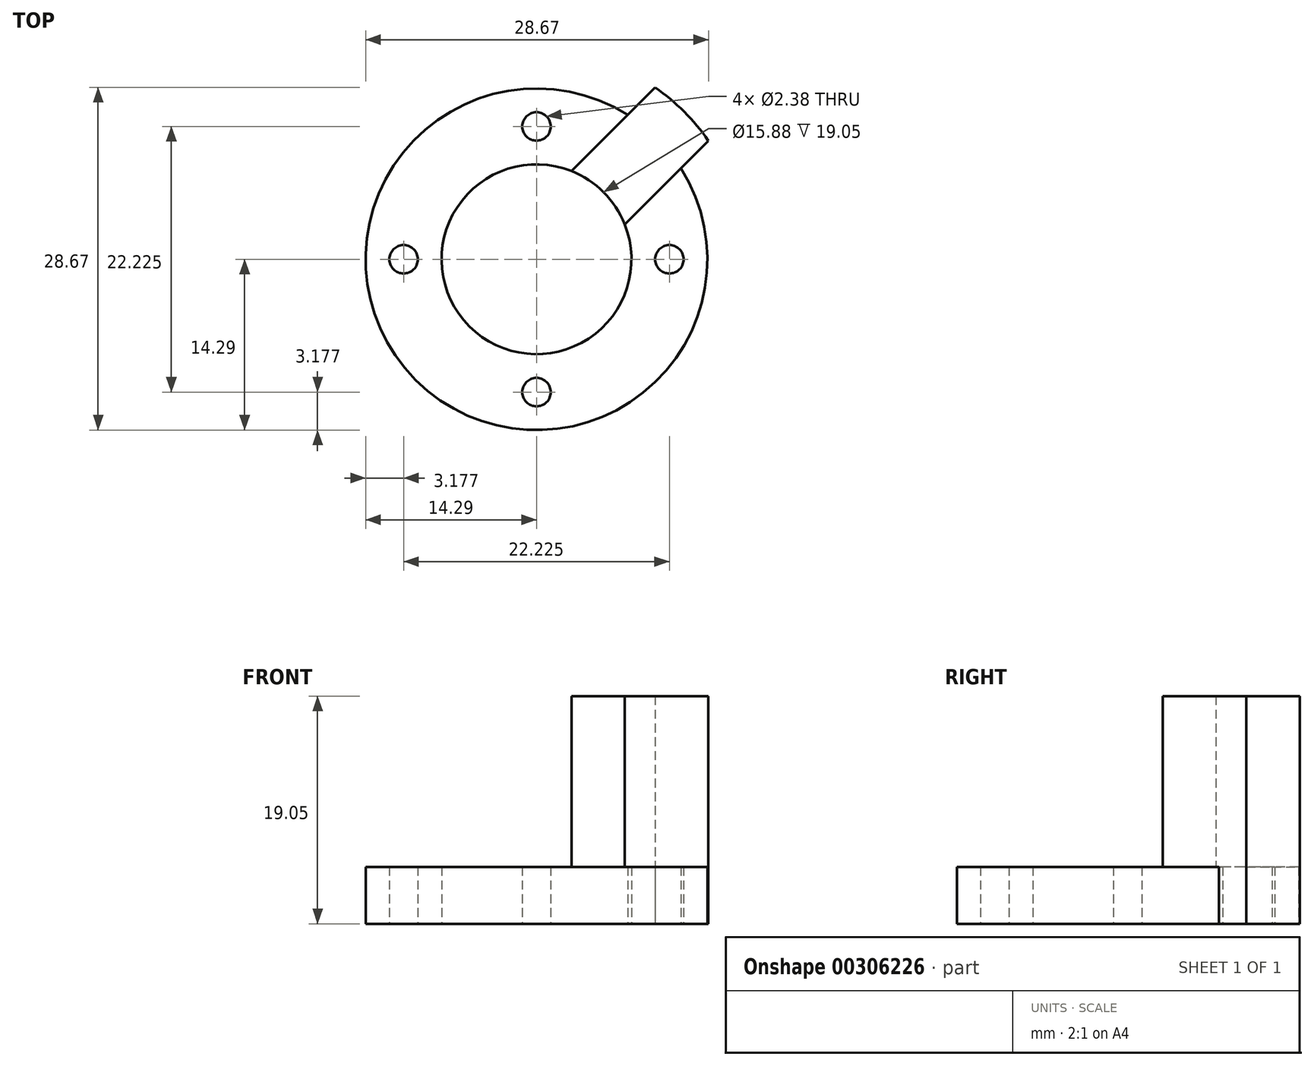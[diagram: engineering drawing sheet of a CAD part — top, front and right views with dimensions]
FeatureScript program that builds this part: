
annotation { "Feature Type Name" : "Feature", "Feature Type Description" : "" }
export const myFeature = defineFeature(function(context is Context, id is Id, definition is map)
    precondition{}
    {
        {
            var Q0;
            Q0=qCreatedBy(makeId("Top.planeOp"),FACE);
            var sketch = newSketch(context, id + "F0", { "sketchPlane" : qUnion([Q0])});
            skCircle(sketch, "E0", {"center": v(0, 0) * mm, "radius": 7.94 * mm});
            skCircle(sketch, "E1", {"center": v(0, 0) * mm, "radius": 14.29 * mm});
            skSolve(sketch);
        }
        {
            var Q0;
            Q0=makeQuery(id+"F0.imprint","IMPRINT",FACE,{"disambiguationData":[TD([[makeQuery(id+"F0.imprint","IMPRINT",EDGE,{"derivedFrom":sQuery(id+"F0.wireOp",EDGE,"E0")}),-1.0]])]});
            extrude(context, id + "F1", {"entities" : qUnion([Q0]), "depth" : 4.76 * mm});
        }
        {
            var Q0;
            Q0=qCreatedBy(makeId("Top.planeOp"),FACE);
            var sketch = newSketch(context, id + "F2", { "sketchPlane" : qUnion([Q0])});
            skCircle(sketch, "E2", {"center": v(0, 0) * mm, "radius": 11.11 * mm, "construction": true});
            skCircle(sketch, "E3", {"center": v(0, 11.11) * mm, "radius": 1.2 * mm});
            skCircle(sketch, "E4", {"center": v(11.11, 0) * mm, "radius": 1.2 * mm});
            skCircle(sketch, "E5", {"center": v(-11.11, 0) * mm, "radius": 1.2 * mm});
            skCircle(sketch, "E6", {"center": v(0, -11.11) * mm, "radius": 1.2 * mm});
            skSolve(sketch);
        }
        {
            var Q0;
            Q0 = qSketchRegion(id + "F2", true);
            extrude(context, id + "F3", {"entities" : qUnion([Q0]), "operationType" : NewBodyOperationType.REMOVE, "depth" : 25.4 * mm});
        }
        {
            var Q0;
            Q0=qCreatedBy(makeId("Top.planeOp"),FACE);
            var sketch = newSketch(context, id + "F4", { "sketchPlane" : qUnion([Q0])});
            skArc(sketch, "E7", {"start": v(14.38, 9.91) * mm, "mid": v(12.35, 12.35) * mm, "end": v(9.91, 14.38) * mm});
            skArc(sketch, "E8", {"start": v(7.38, 2.92) * mm, "mid": v(5.61, 5.61) * mm, "end": v(2.92, 7.38) * mm});
            skLineSegment(sketch, "E9", {"start": v(5.4, 5.4) * mm, "end": v(12.35, 12.35) * mm});
            skLineSegment(sketch, "E10", {"start": v(12.35, 12.35) * mm, "end": v(5.4, 5.4) * mm, "construction": true});
            skLineSegment(sketch, "E11", {"start": v(2.92, 7.38) * mm, "end": v(9.91, 14.38) * mm});
            skLineSegment(sketch, "E12", {"start": v(7.38, 2.92) * mm, "end": v(14.38, 9.91) * mm});
            skSolve(sketch);
        }
        {
            var Q0;
            {var subQ2=sQuery(id+"F4.wireOp",EDGE,"E9");Q0=makeQuery(id+"F4.imprint","IMPRINT",FACE,{"disambiguationData":[TD([[makeQuery(id+"F4.imprint","IMPRINT",EDGE,{"derivedFrom":subQ2}),1.0]])]});}
            var Q1;
            {var subQ2=sQuery(id+"F4.wireOp",EDGE,"E9");Q1=makeQuery(id+"F4.imprint","IMPRINT",FACE,{"disambiguationData":[TD([[makeQuery(id+"F4.imprint","IMPRINT",EDGE,{"derivedFrom":subQ2}),-1.0]])]});}
            extrude(context, id + "F5", {"entities" : qUnion([Q0, Q1]), "operationType" : NewBodyOperationType.ADD, "depth" : 19.05 * mm});
        }
    });
